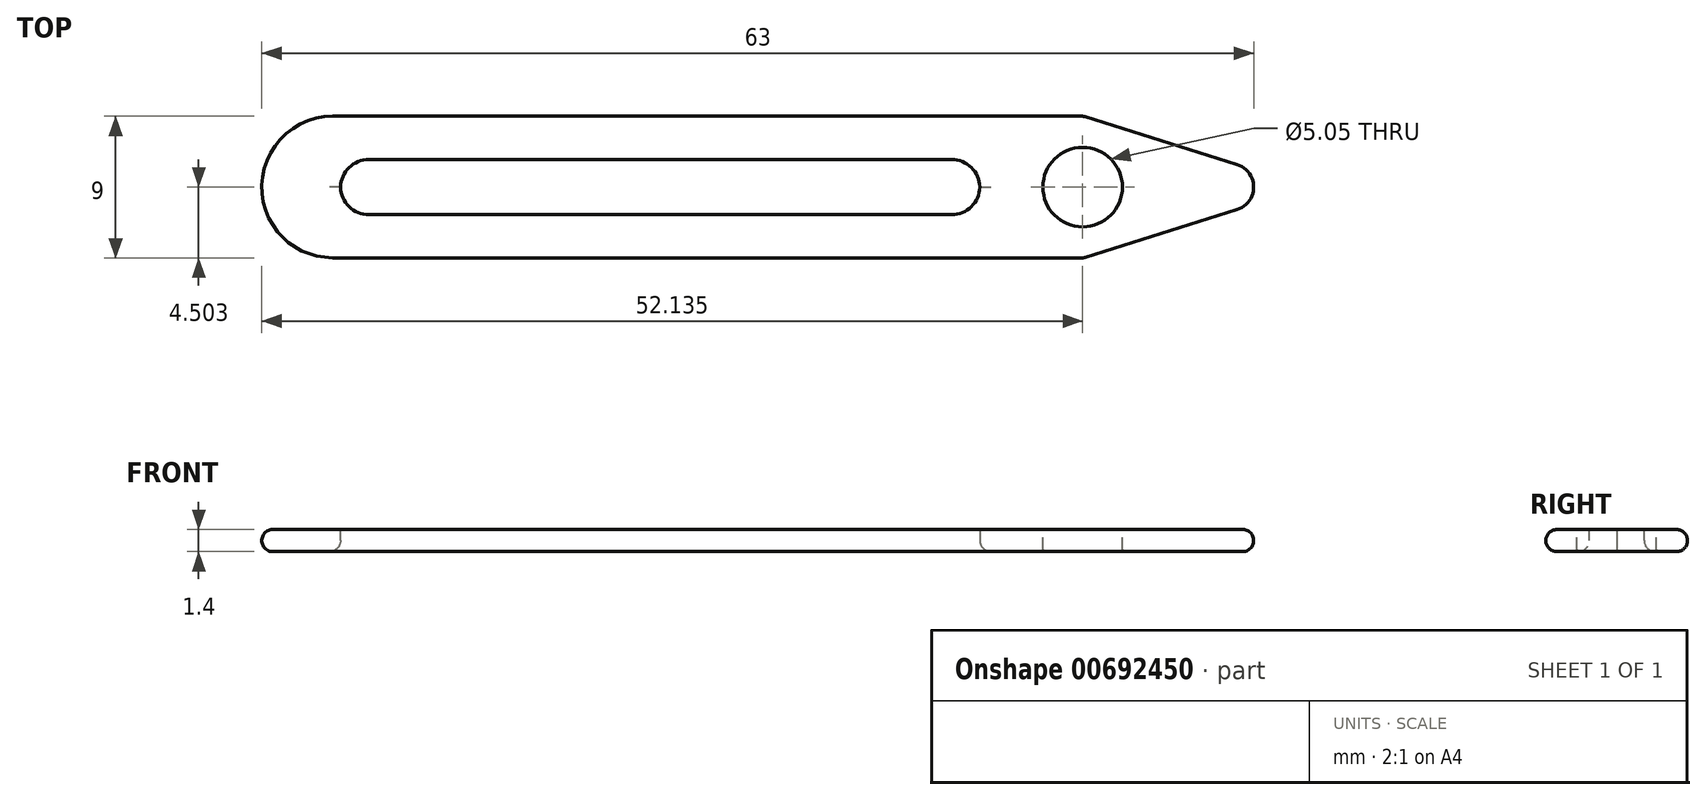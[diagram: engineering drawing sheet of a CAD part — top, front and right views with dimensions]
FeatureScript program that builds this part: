
annotation { "Feature Type Name" : "Feature", "Feature Type Description" : "" }
export const myFeature = defineFeature(function(context is Context, id is Id, definition is map)
    precondition{}
    {
        {
            var Q0;
            Q0=qCreatedBy(makeId("Top.planeOp"),FACE);
            var sketch = newSketch(context, id + "F0", { "sketchPlane" : qUnion([Q0])});
            skLineSegment(sketch, "E0", {"start": v(-29.94, 7.7) * mm, "end": v(17.75, 7.7) * mm});
            skLineSegment(sketch, "E1", {"start": v(17.75, 7.7) * mm, "end": v(32.06, 3.2) * mm});
            skLineSegment(sketch, "E2", {"start": v(17.75, -1.3) * mm, "end": v(32.06, 3.2) * mm});
            skLineSegment(sketch, "E3", {"start": v(-29.94, -1.3) * mm, "end": v(17.75, -1.3) * mm});
            skArc(sketch, "E4", {"start": v(-29.94, 7.7) * mm, "mid": v(-34.44, 3.2) * mm, "end": v(-29.94, -1.3) * mm});
            skSolve(sketch);
        }
        {
            var Q0;
            Q0=makeQuery(id+"F0.imprint","IMPRINT",FACE,{"disambiguationData":[TD([[makeQuery(id+"F0.imprint","IMPRINT",EDGE,{"derivedFrom":sQuery(id+"F0.wireOp",EDGE,"E0")}),-1.0]])]});
            extrude(context, id + "F1", {"entities" : qUnion([Q0]), "depth" : 1.4 * mm, "offsetDistance" : 25 * mm});
        }
        {
            var Q0;
            Q0=makeQuery(id+"F1.opExtrude","SWEPT_EDGE",EDGE,{"disambiguationData":[OSD([sQuery(id+"F0.wireOp",EDGE,"E1"),sQuery(id+"F0.wireOp",EDGE,"E2")])]});
            fillet(context, id + "F2", {"entities" : qUnion([Q0]), "radius" : 1.5 * mm, "tangentPropagation" : true, "allowEdgeOverflow" : false});
        }
        {
            var Q0;
            Q0=makeQuery(id+"F1.opExtrude","CAP_FACE",FACE,{"disambiguationData":[OSD([sQuery(id+"F0.wireOp",EDGE,"E0"),sQuery(id+"F0.wireOp",EDGE,"E1"),sQuery(id+"F0.wireOp",EDGE,"E2"),sQuery(id+"F0.wireOp",EDGE,"E3"),sQuery(id+"F0.wireOp",EDGE,"E4")])],"isStart":false});
            var sketch = newSketch(context, id + "F3", { "sketchPlane" : qUnion([Q0])});
            skCircle(sketch, "E5", {"center": v(17.7, 3.2) * mm, "radius": 2.52 * mm});
            skLineSegment(sketch, "E6.bottom", {"start": v(-29.44, 4.94) * mm, "end": v(11.17, 4.94) * mm});
            skLineSegment(sketch, "E6.top", {"start": v(-29.44, 1.44) * mm, "end": v(11.17, 1.44) * mm});
            skLineSegment(sketch, "E6.left", {"start": v(-29.44, 4.94) * mm, "end": v(-29.44, 1.44) * mm});
            skLineSegment(sketch, "E6.right", {"start": v(11.17, 4.94) * mm, "end": v(11.17, 1.44) * mm});
            skPoint(sketch, "E6.middle", {"position": v(-9.14, 3.2) * mm});
            skSolve(sketch);
        }
        {
            var Q0;
            Q0=makeQuery(id+"F3.imprint","IMPRINT",FACE,{"disambiguationData":[TD([[makeQuery(id+"F3.imprint","IMPRINT",EDGE,{"derivedFrom":sQuery(id+"F3.wireOp",EDGE,"E5")}),1.0]])]});
            var Q1;
            Q1=makeQuery(id+"F3.imprint","IMPRINT",FACE,{"disambiguationData":[TD([[makeQuery(id+"F3.imprint","IMPRINT",EDGE,{"derivedFrom":sQuery(id+"F3.wireOp",EDGE,"E6.bottom")}),-1.0]])]});
            extrude(context, id + "F4", {"entities" : qUnion([Q0, Q1]), "operationType" : NewBodyOperationType.REMOVE, "endBound" : BoundingType.THROUGH_ALL, "oppositeDirection" : true, "depth" : -1 * mm, "offsetDistance" : 25 * mm});
        }
        {
            var Q0;
            Q0=makeQuery(id+"F4.boolean.opBoolean","COPY",EDGE,{"derivedFrom":makeQuery(id+"F4.opExtrude","SWEPT_EDGE",EDGE,{"disambiguationData":[OSD([sQuery(id+"F3.wireOp",EDGE,"E6.bottom"),sQuery(id+"F3.wireOp",EDGE,"E6.left")])]})});
            var Q1;
            Q1=makeQuery(id+"F4.boolean.opBoolean","COPY",EDGE,{"derivedFrom":makeQuery(id+"F4.opExtrude","SWEPT_EDGE",EDGE,{"disambiguationData":[OSD([sQuery(id+"F3.wireOp",EDGE,"E6.top"),sQuery(id+"F3.wireOp",EDGE,"E6.left")])]})});
            var Q2;
            Q2=makeQuery(id+"F4.boolean.opBoolean","COPY",EDGE,{"derivedFrom":makeQuery(id+"F4.opExtrude","SWEPT_EDGE",EDGE,{"disambiguationData":[OSD([sQuery(id+"F3.wireOp",EDGE,"E6.bottom"),sQuery(id+"F3.wireOp",EDGE,"E6.right")])]})});
            var Q3;
            Q3=makeQuery(id+"F4.boolean.opBoolean","COPY",EDGE,{"derivedFrom":makeQuery(id+"F4.opExtrude","SWEPT_EDGE",EDGE,{"disambiguationData":[OSD([sQuery(id+"F3.wireOp",EDGE,"E6.top"),sQuery(id+"F3.wireOp",EDGE,"E6.right")])]})});
            fillet(context, id + "F5", {"entities" : qUnion([Q0, Q1, Q2, Q3]), "radius" : 1.8 * mm, "tangentPropagation" : true, "allowEdgeOverflow" : false});
        }
        {
            var Q0;
            Q0=makeQuery(id+"F1.opExtrude","CAP_EDGE",EDGE,{"disambiguationData":[OSD([sQuery(id+"F0.wireOp",EDGE,"E4")])],"isStart":false});
            var Q1;
            Q1=makeQuery(id+"F1.opExtrude","CAP_EDGE",EDGE,{"disambiguationData":[OSD([sQuery(id+"F0.wireOp",EDGE,"E4")])],"isStart":true});
            var Q2;
            Q2=makeQuery(id+"F1.opExtrude","SWEPT_FACE",FACE,{"disambiguationData":[OSD([sQuery(id+"F0.wireOp",EDGE,"E0")])]});
            var Q3;
            Q3=makeQuery(id+"F1.opExtrude","SWEPT_EDGE",EDGE,{"disambiguationData":[OSD([sQuery(id+"F0.wireOp",EDGE,"E0"),sQuery(id+"F0.wireOp",EDGE,"E1")])]});
            var Q4;
            Q4=makeQuery(id+"F1.opExtrude","SWEPT_FACE",FACE,{"disambiguationData":[OSD([sQuery(id+"F0.wireOp",EDGE,"E3")])]});
            var Q5;
            Q5=makeQuery(id+"F1.opExtrude","SWEPT_FACE",FACE,{"disambiguationData":[OSD([sQuery(id+"F0.wireOp",EDGE,"E4")])]});
            var Q6;
            Q6=makeQuery(id+"F1.opExtrude","SWEPT_EDGE",EDGE,{"disambiguationData":[OSD([sQuery(id+"F0.wireOp",EDGE,"E3"),sQuery(id+"F0.wireOp",EDGE,"E4")])]});
            var Q7;
            Q7=makeQuery(id+"F1.opExtrude","SWEPT_EDGE",EDGE,{"disambiguationData":[OSD([sQuery(id+"F0.wireOp",EDGE,"E0"),sQuery(id+"F0.wireOp",EDGE,"E4")])]});
            var Q8;
            Q8=makeQuery(id+"F1.opExtrude","CAP_EDGE",EDGE,{"disambiguationData":[OSD([sQuery(id+"F0.wireOp",EDGE,"E0")])],"isStart":true});
            var Q9;
            Q9=makeQuery(id+"F1.opExtrude","SWEPT_EDGE",EDGE,{"disambiguationData":[OSD([sQuery(id+"F0.wireOp",EDGE,"E2"),sQuery(id+"F0.wireOp",EDGE,"E3")])]});
            var Q10;
            Q10=makeQuery(id+"F1.opExtrude","CAP_EDGE",EDGE,{"disambiguationData":[OSD([sQuery(id+"F0.wireOp",EDGE,"E0")])],"isStart":false});
            var Q11;
            Q11=makeQuery(id+"F1.opExtrude","CAP_EDGE",EDGE,{"disambiguationData":[OSD([sQuery(id+"F0.wireOp",EDGE,"E3")])],"isStart":true});
            var Q12;
            Q12=makeQuery(id+"F1.opExtrude","CAP_EDGE",EDGE,{"disambiguationData":[OSD([sQuery(id+"F0.wireOp",EDGE,"E3")])],"isStart":false});
            var Q13;
            Q13=makeQuery(id+"F1.opExtrude","CAP_EDGE",EDGE,{"disambiguationData":[OSD([sQuery(id+"F0.wireOp",EDGE,"E2")])],"isStart":false});
            var Q14;
            Q14=makeQuery(id+"F1.opExtrude","CAP_EDGE",EDGE,{"disambiguationData":[OSD([sQuery(id+"F0.wireOp",EDGE,"E1")])],"isStart":false});
            var Q15;
            Q15=makeQuery(id+"F1.opExtrude","CAP_EDGE",EDGE,{"disambiguationData":[OSD([sQuery(id+"F0.wireOp",EDGE,"E1")])],"isStart":true});
            var Q16;
            Q16=makeQuery(id+"F1.opExtrude","CAP_EDGE",EDGE,{"disambiguationData":[OSD([sQuery(id+"F0.wireOp",EDGE,"E2")])],"isStart":true});
            var Q17;
            {var subQ0=sQuery(id+"F0.wireOp",EDGE,"E2");var subQ1=sQuery(id+"F0.wireOp",EDGE,"E1");Q17=makeQuery(id+"F2.opFillet","BLEND_EDGE",EDGE,{"blendedFrom":[makeQuery(id+"F1.opExtrude","SWEPT_EDGE",EDGE,{"disambiguationData":[OSD([subQ1,subQ0])]}),makeQuery(id+"F1.opExtrude","CAP_FACE",FACE,{"disambiguationData":[OSD([sQuery(id+"F0.wireOp",EDGE,"E0"),subQ1,subQ0,sQuery(id+"F0.wireOp",EDGE,"E3"),sQuery(id+"F0.wireOp",EDGE,"E4")])],"isStart":false})],"blendedInto":[makeQuery(id+"F1.opExtrude","CAP_FACE",FACE,{"disambiguationData":[OSD([sQuery(id+"F0.wireOp",EDGE,"E0"),subQ1,subQ0,sQuery(id+"F0.wireOp",EDGE,"E3"),sQuery(id+"F0.wireOp",EDGE,"E4")])],"isStart":false})]});}
            var Q18;
            {var subQ0=sQuery(id+"F0.wireOp",EDGE,"E2");var subQ1=sQuery(id+"F0.wireOp",EDGE,"E1");Q18=makeQuery(id+"F2.opFillet","BLEND_EDGE",EDGE,{"blendedFrom":[makeQuery(id+"F1.opExtrude","SWEPT_EDGE",EDGE,{"disambiguationData":[OSD([subQ1,subQ0])]}),makeQuery(id+"F1.opExtrude","CAP_FACE",FACE,{"disambiguationData":[OSD([sQuery(id+"F0.wireOp",EDGE,"E0"),subQ1,subQ0,sQuery(id+"F0.wireOp",EDGE,"E3"),sQuery(id+"F0.wireOp",EDGE,"E4")])],"isStart":true})],"blendedInto":[makeQuery(id+"F1.opExtrude","CAP_FACE",FACE,{"disambiguationData":[OSD([sQuery(id+"F0.wireOp",EDGE,"E0"),subQ1,subQ0,sQuery(id+"F0.wireOp",EDGE,"E3"),sQuery(id+"F0.wireOp",EDGE,"E4")])],"isStart":true})]});}
            var Q19;
            Q19=makeQuery(id+"F4.boolean.opBoolean","COPY",EDGE,{"derivedFrom":makeQuery(id+"F4.opExtrude","CAP_EDGE",EDGE,{"disambiguationData":[OSD([sQuery(id+"F3.wireOp",EDGE,"E6.bottom")])],"isStart":true})});
            var Q20;
            Q20=makeQuery(id+"F4.boolean.opBoolean","COPY",EDGE,{"derivedFrom":makeQuery(id+"F4.opExtrude","CAP_EDGE",EDGE,{"disambiguationData":[OSD([sQuery(id+"F3.wireOp",EDGE,"E6.top")])],"isStart":true})});
            var Q21;
            Q21=makeQuery(id+"F4.boolean.opBoolean","INTERSECT",EDGE,{"derivedFrom":[makeQuery(id+"F1.opExtrude","CAP_FACE",FACE,{"disambiguationData":[OSD([sQuery(id+"F0.wireOp",EDGE,"E0"),sQuery(id+"F0.wireOp",EDGE,"E1"),sQuery(id+"F0.wireOp",EDGE,"E2"),sQuery(id+"F0.wireOp",EDGE,"E3"),sQuery(id+"F0.wireOp",EDGE,"E4")])],"isStart":true}),makeQuery(id+"F4.opExtrude","SWEPT_FACE",FACE,{"disambiguationData":[OSD([sQuery(id+"F3.wireOp",EDGE,"E6.bottom")])]})]});
            var Q22;
            Q22=makeQuery(id+"F4.boolean.opBoolean","INTERSECT",EDGE,{"derivedFrom":[makeQuery(id+"F1.opExtrude","CAP_FACE",FACE,{"disambiguationData":[OSD([sQuery(id+"F0.wireOp",EDGE,"E0"),sQuery(id+"F0.wireOp",EDGE,"E1"),sQuery(id+"F0.wireOp",EDGE,"E2"),sQuery(id+"F0.wireOp",EDGE,"E3"),sQuery(id+"F0.wireOp",EDGE,"E4")])],"isStart":true}),makeQuery(id+"F4.opExtrude","SWEPT_FACE",FACE,{"disambiguationData":[OSD([sQuery(id+"F3.wireOp",EDGE,"E6.top")])]})]});
            fillet(context, id + "F6", {"entities" : qUnion([Q0, Q1, Q2, Q3, Q4, Q5, Q6, Q7, Q8, Q9, Q10, Q11, Q12, Q13, Q14, Q15, Q16, Q17, Q18, Q19, Q20, Q21, Q22]), "radius" : .7 * mm, "tangentPropagation" : true, "allowEdgeOverflow" : false});
        }
        {
            var Q0;
            Q0=makeQuery(id+"F4.boolean.opBoolean","COPY",EDGE,{"derivedFrom":makeQuery(id+"F4.opExtrude","CAP_EDGE",EDGE,{"disambiguationData":[OSD([sQuery(id+"F3.wireOp",EDGE,"E5")])],"isStart":true})});
            var Q1;
            Q1=makeQuery(id+"F4.boolean.opBoolean","INTERSECT",EDGE,{"derivedFrom":[makeQuery(id+"F1.opExtrude","CAP_FACE",FACE,{"disambiguationData":[OSD([sQuery(id+"F0.wireOp",EDGE,"E0"),sQuery(id+"F0.wireOp",EDGE,"E1"),sQuery(id+"F0.wireOp",EDGE,"E2"),sQuery(id+"F0.wireOp",EDGE,"E3"),sQuery(id+"F0.wireOp",EDGE,"E4")])],"isStart":true}),makeQuery(id+"F4.opExtrude","SWEPT_FACE",FACE,{"disambiguationData":[OSD([sQuery(id+"F3.wireOp",EDGE,"E5")])]})]});
            fillet(context, id + "F7", {"entities" : qUnion([Q0, Q1]), "radius" : 0.15 * mm, "tangentPropagation" : true, "allowEdgeOverflow" : false});
        }
    });
